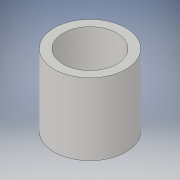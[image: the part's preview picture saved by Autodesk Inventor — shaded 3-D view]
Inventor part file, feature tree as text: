
AUTODESK INVENTOR PART (.ipt)
format: ipt  version: 2019 (Build 230136000, 136)  size: 94,720 bytes
history: native  units: mm
features: extrude x1, sketch x1
ambient origin geometry x8: Origin, YZ Plane, XZ Plane, XY Plane, X Axis, Y Axis, Z Axis, Center Point
bodies: Solid1 (feature_tree)
feature tree (2):
  extrude  "Extrusion1"  Depth=20.0mm
  sketch  "Sketch1"  dims[d0=15.0mm d1=20.0mm d2=20.0mm d3=0.0mm]
